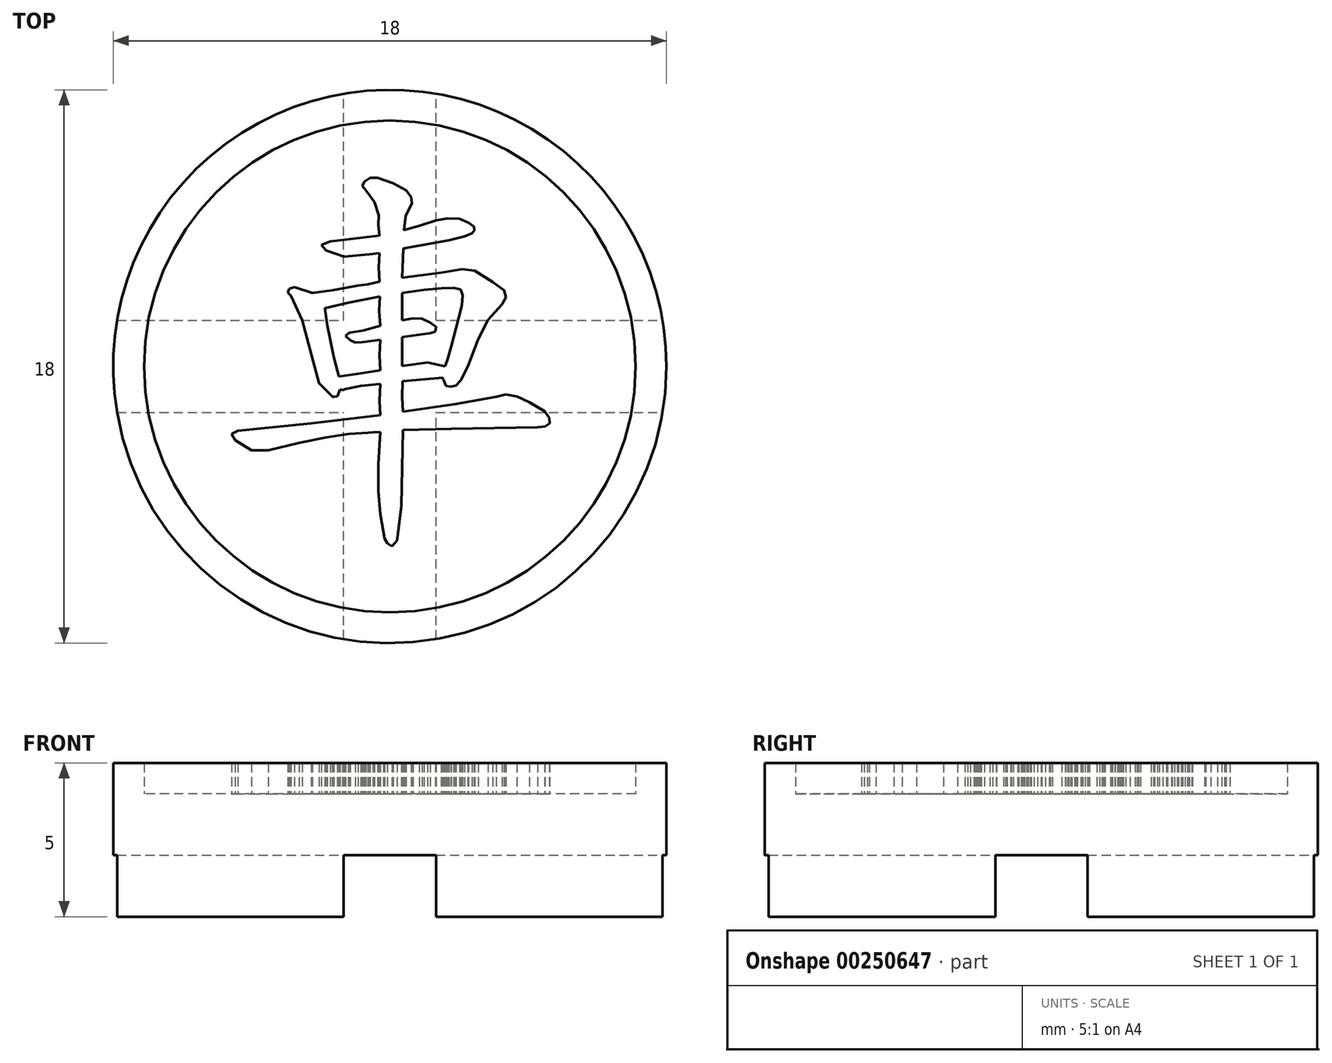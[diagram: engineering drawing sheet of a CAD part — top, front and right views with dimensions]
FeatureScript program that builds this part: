
annotation { "Feature Type Name" : "Feature", "Feature Type Description" : "" }
export const myFeature = defineFeature(function(context is Context, id is Id, definition is map)
    precondition{}
    {
        {
            var Q0;
            Q0=qCreatedBy(makeId("Top.planeOp"),FACE);
            var sketch = newSketch(context, id + "F0", { "sketchPlane" : qUnion([Q0]), "disableImprinting" : false});
            skCircle(sketch, "E0", {"center": v(-31.33, 19.76) * mm, "radius": 9 * mm});
            skSolve(sketch);
        }
        {
            var Q0;
            Q0=qSketchRegion(id+"F0",true);
            extrude(context, id + "F1", {"entities" : qUnion([Q0]), "flatOperationType" : FlatOperationType.REMOVE, "offsetDistance" : 25 * mm, "depth" : 4 * mm, "domain" : OperationDomain.MODEL});
        }
        {
            var Q0;
            Q0=makeQuery(id+"F1.opExtrude","CAP_FACE",FACE,{"disambiguationData":[OSD([sQuery(id+"F0.wireOp",EDGE,"E0")])],"isStart":false});
            var sketch = newSketch(context, id + "F2", { "sketchPlane" : qUnion([Q0]), "disableImprinting" : false});
            skCircle(sketch, "E1", {"center": v(-31.33, 19.76) * mm, "radius": 8 * mm});
            skCircle(sketch, "E2", {"center": v(-31.33, 19.76) * mm, "radius": 9 * mm});
            skSolve(sketch);
        }
        {
            var Q0;
            Q0=makeQuery(id+"F1.opExtrude","CAP_FACE",FACE,{"disambiguationData":[OSD([sQuery(id+"F0.wireOp",EDGE,"E0")])],"isStart":true});
            var sketch = newSketch(context, id + "F3", { "sketchPlane" : qUnion([Q0]), "disableImprinting" : false});
            skLineSegment(sketch, "E3", {"start": v(-31.33, -19.76) * mm, "end": v(-22.33, -19.76) * mm, "construction": true});
            skLineSegment(sketch, "E4", {"start": v(-31.33, -19.76) * mm, "end": v(-31.33, -10.76) * mm, "construction": true});
            skLineSegment(sketch, "E5", {"start": v(-31.33, -19.76) * mm, "end": v(-40.33, -19.76) * mm, "construction": true});
            skLineSegment(sketch, "E6", {"start": v(-31.33, -19.76) * mm, "end": v(-31.33, -28.76) * mm, "construction": true});
            skLineSegment(sketch, "E7.bottom", {"start": v(-40.33, -28.76) * mm, "end": v(-22.33, -28.76) * mm});
            skLineSegment(sketch, "E7.top", {"start": v(-40.33, -10.76) * mm, "end": v(-22.33, -10.76) * mm});
            skLineSegment(sketch, "E7.left", {"start": v(-22.33, -10.76) * mm, "end": v(-22.33, -28.76) * mm});
            skLineSegment(sketch, "E7.right", {"start": v(-40.33, -10.76) * mm, "end": v(-40.33, -28.76) * mm});
            skPoint(sketch, "E8", {"position": v(-31.33, -28.76) * mm});
            skPoint(sketch, "E9", {"position": v(-40.33, -19.76) * mm});
            skPoint(sketch, "E10", {"position": v(-22.33, -19.76) * mm});
            skPoint(sketch, "E11", {"position": v(-31.33, -10.76) * mm});
            skLineSegment(sketch, "E12.bottom", {"start": v(-32.83, -10.76) * mm, "end": v(-29.83, -10.76) * mm});
            skLineSegment(sketch, "E12.top", {"start": v(-32.83, -28.76) * mm, "end": v(-29.83, -28.76) * mm});
            skLineSegment(sketch, "E12.left", {"start": v(-32.83, -10.76) * mm, "end": v(-32.83, -28.76) * mm});
            skLineSegment(sketch, "E12.right", {"start": v(-29.83, -10.76) * mm, "end": v(-29.83, -28.76) * mm});
            skLineSegment(sketch, "E13.bottom", {"start": v(-40.33, -18.26) * mm, "end": v(-22.33, -18.26) * mm});
            skLineSegment(sketch, "E13.top", {"start": v(-40.33, -21.26) * mm, "end": v(-22.33, -21.26) * mm});
            skLineSegment(sketch, "E13.left", {"start": v(-40.33, -18.26) * mm, "end": v(-40.33, -21.26) * mm});
            skLineSegment(sketch, "E13.right", {"start": v(-22.33, -18.26) * mm, "end": v(-22.33, -21.26) * mm});
            skSolve(sketch);
        }
        {
            var Q0;
            {var subQ1=sQuery(id+"F3.wireOp",EDGE,"E12.bottom");var subQ3=makeQuery(id+"F1.opExtrude","CAP_EDGE",EDGE,{"disambiguationData":[OSD([sQuery(id+"F0.wireOp",EDGE,"E0")])],"isStart":true});var subQ4=makeQuery(id+"F3.imprint","INTERSECT",VERTEX,{"derivedFrom":[subQ3,subQ1]});Q0=makeQuery(id+"F3.imprint","IMPRINT",FACE,{"disambiguationData":[TD([[makeQuery(id+"F3.imprint","IMPRINT",EDGE,{"disambiguationData":[TD([[subQ4,1.0]])],"derivedFrom":subQ3}),1.0]])]});}
            var Q1;
            {var subQ1=sQuery(id+"F3.wireOp",EDGE,"E12.bottom");var subQ3=makeQuery(id+"F1.opExtrude","CAP_EDGE",EDGE,{"disambiguationData":[OSD([sQuery(id+"F0.wireOp",EDGE,"E0")])],"isStart":true});var subQ4=makeQuery(id+"F3.imprint","INTERSECT",VERTEX,{"derivedFrom":[subQ3,subQ1]});Q1=makeQuery(id+"F3.imprint","IMPRINT",FACE,{"disambiguationData":[TD([[makeQuery(id+"F3.imprint","IMPRINT",EDGE,{"disambiguationData":[TD([[subQ4,-1.0]])],"derivedFrom":subQ3}),1.0]])]});}
            var Q2;
            {var subQ1=sQuery(id+"F3.wireOp",EDGE,"E12.top");var subQ3=makeQuery(id+"F1.opExtrude","CAP_EDGE",EDGE,{"disambiguationData":[OSD([sQuery(id+"F0.wireOp",EDGE,"E0")])],"isStart":true});var subQ4=makeQuery(id+"F3.imprint","INTERSECT",VERTEX,{"derivedFrom":[subQ3,subQ1]});Q2=makeQuery(id+"F3.imprint","IMPRINT",FACE,{"disambiguationData":[TD([[makeQuery(id+"F3.imprint","IMPRINT",EDGE,{"disambiguationData":[TD([[subQ4,-1.0]])],"derivedFrom":subQ3}),1.0]])]});}
            var Q3;
            {var subQ1=sQuery(id+"F3.wireOp",EDGE,"E12.top");var subQ3=makeQuery(id+"F1.opExtrude","CAP_EDGE",EDGE,{"disambiguationData":[OSD([sQuery(id+"F0.wireOp",EDGE,"E0")])],"isStart":true});var subQ4=makeQuery(id+"F3.imprint","INTERSECT",VERTEX,{"derivedFrom":[subQ3,subQ1]});Q3=makeQuery(id+"F3.imprint","IMPRINT",FACE,{"disambiguationData":[TD([[makeQuery(id+"F3.imprint","IMPRINT",EDGE,{"disambiguationData":[TD([[subQ4,1.0]])],"derivedFrom":subQ3}),1.0]])]});}
            var Q4;
            {var subQ0=sQuery(id+"F3.wireOp",EDGE,"E13.left");var subQ3=makeQuery(id+"F1.opExtrude","CAP_EDGE",EDGE,{"disambiguationData":[OSD([sQuery(id+"F0.wireOp",EDGE,"E0")])],"isStart":true});var subQ5=makeQuery(id+"F3.imprint","INTERSECT",VERTEX,{"derivedFrom":[subQ3,subQ0]});Q4=makeQuery(id+"F3.imprint","IMPRINT",FACE,{"disambiguationData":[TD([[makeQuery(id+"F3.imprint","IMPRINT",EDGE,{"disambiguationData":[TD([[subQ5,-1.0]])],"derivedFrom":subQ3}),1.0]])]});}
            var Q5;
            {var subQ0=sQuery(id+"F3.wireOp",EDGE,"E13.right");var subQ3=makeQuery(id+"F1.opExtrude","CAP_EDGE",EDGE,{"disambiguationData":[OSD([sQuery(id+"F0.wireOp",EDGE,"E0")])],"isStart":true});var subQ5=makeQuery(id+"F3.imprint","INTERSECT",VERTEX,{"derivedFrom":[subQ3,subQ0]});Q5=makeQuery(id+"F3.imprint","IMPRINT",FACE,{"disambiguationData":[TD([[makeQuery(id+"F3.imprint","IMPRINT",EDGE,{"disambiguationData":[TD([[subQ5,1.0]])],"derivedFrom":subQ3}),1.0]])]});}
            var Q6;
            {var subQ0=sQuery(id+"F3.wireOp",EDGE,"E13.left");var subQ3=makeQuery(id+"F1.opExtrude","CAP_EDGE",EDGE,{"disambiguationData":[OSD([sQuery(id+"F0.wireOp",EDGE,"E0")])],"isStart":true});var subQ5=makeQuery(id+"F3.imprint","INTERSECT",VERTEX,{"derivedFrom":[subQ3,subQ0]});Q6=makeQuery(id+"F3.imprint","IMPRINT",FACE,{"disambiguationData":[TD([[makeQuery(id+"F3.imprint","IMPRINT",EDGE,{"disambiguationData":[TD([[subQ5,1.0]])],"derivedFrom":subQ3}),1.0]])]});}
            var Q7;
            {var subQ0=sQuery(id+"F3.wireOp",EDGE,"E13.right");var subQ3=makeQuery(id+"F1.opExtrude","CAP_EDGE",EDGE,{"disambiguationData":[OSD([sQuery(id+"F0.wireOp",EDGE,"E0")])],"isStart":true});var subQ5=makeQuery(id+"F3.imprint","INTERSECT",VERTEX,{"derivedFrom":[subQ3,subQ0]});Q7=makeQuery(id+"F3.imprint","IMPRINT",FACE,{"disambiguationData":[TD([[makeQuery(id+"F3.imprint","IMPRINT",EDGE,{"disambiguationData":[TD([[subQ5,-1.0]])],"derivedFrom":subQ3}),1.0]])]});}
            var Q8;
            {var subQ3=makeQuery(id+"F1.opExtrude","CAP_EDGE",EDGE,{"disambiguationData":[OSD([sQuery(id+"F0.wireOp",EDGE,"E0")])],"isStart":true});var subQ5=sQuery(id+"F3.wireOp",EDGE,"E12.left");var subQ8=makeQuery(id+"F3.imprint","INTERSECT",VERTEX,{"disambiguationData":[OD(1.0)],"derivedFrom":[subQ3,subQ5]});Q8=makeQuery(id+"F3.imprint","IMPRINT",FACE,{"disambiguationData":[TD([[makeQuery(id+"F3.imprint","IMPRINT",EDGE,{"disambiguationData":[TD([[subQ8,-1.0]])],"derivedFrom":subQ3}),1.0]])]});}
            var Q9;
            {var subQ3=makeQuery(id+"F1.opExtrude","CAP_EDGE",EDGE,{"disambiguationData":[OSD([sQuery(id+"F0.wireOp",EDGE,"E0")])],"isStart":true});var subQ5=sQuery(id+"F3.wireOp",EDGE,"E12.right");var subQ8=makeQuery(id+"F3.imprint","INTERSECT",VERTEX,{"disambiguationData":[OD(1.0)],"derivedFrom":[subQ3,subQ5]});Q9=makeQuery(id+"F3.imprint","IMPRINT",FACE,{"disambiguationData":[TD([[makeQuery(id+"F3.imprint","IMPRINT",EDGE,{"disambiguationData":[TD([[subQ8,1.0]])],"derivedFrom":subQ3}),1.0]])]});}
            var Q10;
            {var subQ3=makeQuery(id+"F1.opExtrude","CAP_EDGE",EDGE,{"disambiguationData":[OSD([sQuery(id+"F0.wireOp",EDGE,"E0")])],"isStart":true});var subQ5=sQuery(id+"F3.wireOp",EDGE,"E12.left");var subQ8=makeQuery(id+"F3.imprint","INTERSECT",VERTEX,{"disambiguationData":[OD(0.0)],"derivedFrom":[subQ3,subQ5]});Q10=makeQuery(id+"F3.imprint","IMPRINT",FACE,{"disambiguationData":[TD([[makeQuery(id+"F3.imprint","IMPRINT",EDGE,{"disambiguationData":[TD([[subQ8,1.0]])],"derivedFrom":subQ3}),1.0]])]});}
            var Q11;
            {var subQ3=makeQuery(id+"F1.opExtrude","CAP_EDGE",EDGE,{"disambiguationData":[OSD([sQuery(id+"F0.wireOp",EDGE,"E0")])],"isStart":true});var subQ5=sQuery(id+"F3.wireOp",EDGE,"E12.right");var subQ8=makeQuery(id+"F3.imprint","INTERSECT",VERTEX,{"disambiguationData":[OD(0.0)],"derivedFrom":[subQ3,subQ5]});Q11=makeQuery(id+"F3.imprint","IMPRINT",FACE,{"disambiguationData":[TD([[makeQuery(id+"F3.imprint","IMPRINT",EDGE,{"disambiguationData":[TD([[subQ8,-1.0]])],"derivedFrom":subQ3}),1.0]])]});}
            var Q12;
            {var subQ2=sQuery(id+"F3.wireOp",EDGE,"E12.left");var subQ4=sQuery(id+"F3.wireOp",EDGE,"E13.bottom");var subQ8=makeQuery(id+"F3.imprint","INTERSECT",VERTEX,{"derivedFrom":[subQ2,subQ4]});Q12=makeQuery(id+"F3.imprint","IMPRINT",FACE,{"disambiguationData":[TD([[makeQuery(id+"F3.imprint","IMPRINT",EDGE,{"disambiguationData":[TD([[subQ8,1.0]])],"derivedFrom":subQ2}),1.0]])]});}
            var Q13;
            {var subQ1=sQuery(id+"F3.wireOp",EDGE,"E12.left");var subQ5=sQuery(id+"F3.wireOp",EDGE,"E13.bottom");var subQ6=makeQuery(id+"F3.imprint","INTERSECT",VERTEX,{"derivedFrom":[subQ1,subQ5]});Q13=makeQuery(id+"F3.imprint","IMPRINT",FACE,{"disambiguationData":[TD([[makeQuery(id+"F3.imprint","IMPRINT",EDGE,{"disambiguationData":[TD([[subQ6,-1.0]])],"derivedFrom":subQ1}),-1.0]])]});}
            var Q14;
            {var subQ0=sQuery(id+"F3.wireOp",EDGE,"E13.top");var subQ1=sQuery(id+"F3.wireOp",EDGE,"E12.left");var subQ2=makeQuery(id+"F3.imprint","INTERSECT",VERTEX,{"derivedFrom":[subQ1,subQ0]});Q14=makeQuery(id+"F3.imprint","IMPRINT",FACE,{"disambiguationData":[TD([[makeQuery(id+"F3.imprint","IMPRINT",EDGE,{"disambiguationData":[TD([[subQ2,-1.0]])],"derivedFrom":subQ1}),1.0]])]});}
            var Q15;
            {var subQ2=sQuery(id+"F3.wireOp",EDGE,"E13.bottom");var subQ5=sQuery(id+"F3.wireOp",EDGE,"E12.right");var subQ8=makeQuery(id+"F3.imprint","INTERSECT",VERTEX,{"derivedFrom":[subQ5,subQ2]});Q15=makeQuery(id+"F3.imprint","IMPRINT",FACE,{"disambiguationData":[TD([[makeQuery(id+"F3.imprint","IMPRINT",EDGE,{"disambiguationData":[TD([[subQ8,-1.0]])],"derivedFrom":subQ5}),1.0]])]});}
            var Q16;
            {var subQ0=sQuery(id+"F3.wireOp",EDGE,"E13.bottom");var subQ1=sQuery(id+"F3.wireOp",EDGE,"E12.left");var subQ2=makeQuery(id+"F3.imprint","INTERSECT",VERTEX,{"derivedFrom":[subQ1,subQ0]});Q16=makeQuery(id+"F3.imprint","IMPRINT",FACE,{"disambiguationData":[TD([[makeQuery(id+"F3.imprint","IMPRINT",EDGE,{"disambiguationData":[TD([[subQ2,-1.0]])],"derivedFrom":subQ1}),1.0]])]});}
            extrude(context, id + "F4", {"entities" : qUnion([Q0, Q1, Q2, Q3, Q4, Q5, Q6, Q7, Q8, Q9, Q10, Q11, Q12, Q13, Q14, Q15, Q16]), "operationType" : NewBodyOperationType.REMOVE, "oppositeDirection" : true, "depth" : 2 * mm});
        }
        {
            var Q0;
            Q0=qSketchRegion(id+"F2",true);
            var Q1;
            Q1=makeQuery(id+"F2.imprint","IMPRINT",FACE,{"disambiguationData":[TD([[makeQuery(id+"F2.imprint","IMPRINT",EDGE,{"derivedFrom":sQuery(id+"F2.wireOp",EDGE,"hKqnuJLd-dfdz-vJIs-yDKo-c4hLNRw30SuP")}),-1.0]])]});
            extrude(context, id + "F5", {"entities" : qUnion([Q0, Q1]), "operationType" : NewBodyOperationType.ADD, "depth" : 1 * mm});
        }
        {
            var Q0;
            Q0=makeQuery(id+"F1.opExtrude","CAP_FACE",FACE,{"disambiguationData":[OSD([sQuery(id+"F0.wireOp",EDGE,"E0")])],"isStart":false});
            var sketch = newSketch(context, id + "F6", { "sketchPlane" : qUnion([Q0])});
            skLineSegment(sketch, "E14", {"start": v(-31.65, 17.63) * mm, "end": v(-31.7, 16.58) * mm});
            skLineSegment(sketch, "E15", {"start": v(-31.7, 16.58) * mm, "end": v(-31.7, 15.7) * mm});
            skLineSegment(sketch, "E16", {"start": v(-31.7, 15.7) * mm, "end": v(-31.64, 14.96) * mm});
            skLineSegment(sketch, "E17", {"start": v(-31.64, 14.96) * mm, "end": v(-31.55, 14.38) * mm});
            skLineSegment(sketch, "E18", {"start": v(-31.55, 14.38) * mm, "end": v(-31.5, 14.16) * mm});
            skLineSegment(sketch, "E19", {"start": v(-31.5, 14.16) * mm, "end": v(-31.4, 14) * mm});
            skLineSegment(sketch, "E20", {"start": v(-31.4, 14) * mm, "end": v(-31.26, 13.9) * mm});
            skLineSegment(sketch, "E21", {"start": v(-31.26, 13.9) * mm, "end": v(-31.1, 14.1) * mm});
            skLineSegment(sketch, "E22", {"start": v(-31.1, 14.1) * mm, "end": v(-30.96, 15.23) * mm});
            skLineSegment(sketch, "E23", {"start": v(-30.96, 15.23) * mm, "end": v(-30.9, 17.69) * mm});
            skLineSegment(sketch, "E24", {"start": v(-30.9, 17.69) * mm, "end": v(-29.33, 17.73) * mm});
            skLineSegment(sketch, "E25", {"start": v(-29.33, 17.73) * mm, "end": v(-26.52, 17.78) * mm});
            skLineSegment(sketch, "E26", {"start": v(-26.52, 17.78) * mm, "end": v(-26.28, 17.8) * mm});
            skLineSegment(sketch, "E27", {"start": v(-26.28, 17.8) * mm, "end": v(-26.13, 17.9) * mm});
            skLineSegment(sketch, "E28", {"start": v(-26.13, 17.9) * mm, "end": v(-26.14, 18.08) * mm});
            skLineSegment(sketch, "E29", {"start": v(-26.14, 18.08) * mm, "end": v(-26.3, 18.3) * mm});
            skLineSegment(sketch, "E30", {"start": v(-26.3, 18.3) * mm, "end": v(-26.78, 18.6) * mm});
            skLineSegment(sketch, "E31", {"start": v(-26.78, 18.6) * mm, "end": v(-27.2, 18.78) * mm});
            skLineSegment(sketch, "E32", {"start": v(-27.2, 18.78) * mm, "end": v(-27.56, 18.84) * mm});
            skLineSegment(sketch, "E33", {"start": v(-27.56, 18.84) * mm, "end": v(-27.87, 18.77) * mm});
            skLineSegment(sketch, "E34", {"start": v(-27.87, 18.77) * mm, "end": v(-29.23, 18.53) * mm});
            skLineSegment(sketch, "E35", {"start": v(-29.23, 18.53) * mm, "end": v(-30.9, 18.3) * mm});
            skLineSegment(sketch, "E36", {"start": v(-30.9, 18.3) * mm, "end": v(-30.93, 18.76) * mm});
            skLineSegment(sketch, "E37", {"start": v(-30.93, 18.76) * mm, "end": v(-30.92, 19.28) * mm});
            skLineSegment(sketch, "E38", {"start": v(-30.92, 19.28) * mm, "end": v(-29.6, 19.4) * mm});
            skLineSegment(sketch, "E39", {"start": v(-29.6, 19.4) * mm, "end": v(-29.61, 19.33) * mm});
            skLineSegment(sketch, "E40", {"start": v(-29.61, 19.33) * mm, "end": v(-29.58, 19.31) * mm});
            skLineSegment(sketch, "E41", {"start": v(-29.58, 19.31) * mm, "end": v(-29.51, 19.13) * mm});
            skLineSegment(sketch, "E42", {"start": v(-29.51, 19.13) * mm, "end": v(-29.34, 19.1) * mm});
            skLineSegment(sketch, "E43", {"start": v(-29.34, 19.1) * mm, "end": v(-29.18, 19.15) * mm});
            skLineSegment(sketch, "E44", {"start": v(-29.18, 19.15) * mm, "end": v(-29.03, 19.31) * mm});
            skLineSegment(sketch, "E45", {"start": v(-29.03, 19.31) * mm, "end": v(-28.8, 19.75) * mm});
            skLineSegment(sketch, "E46", {"start": v(-28.8, 19.75) * mm, "end": v(-28.46, 20.65) * mm});
            skLineSegment(sketch, "E47", {"start": v(-28.46, 20.65) * mm, "end": v(-28.14, 21.28) * mm});
            skLineSegment(sketch, "E48", {"start": v(-28.14, 21.28) * mm, "end": v(-27.68, 21.79) * mm});
            skLineSegment(sketch, "E49", {"start": v(-27.68, 21.79) * mm, "end": v(-27.55, 22) * mm});
            skLineSegment(sketch, "E50", {"start": v(-27.55, 22) * mm, "end": v(-27.62, 22.24) * mm});
            skLineSegment(sketch, "E51", {"start": v(-27.62, 22.24) * mm, "end": v(-27.98, 22.5) * mm});
            skLineSegment(sketch, "E52", {"start": v(-27.98, 22.5) * mm, "end": v(-28.57, 22.88) * mm});
            skLineSegment(sketch, "E53", {"start": v(-28.57, 22.88) * mm, "end": v(-28.97, 22.93) * mm});
            skLineSegment(sketch, "E54", {"start": v(-28.97, 22.93) * mm, "end": v(-29.66, 22.81) * mm});
            skLineSegment(sketch, "E55", {"start": v(-29.66, 22.81) * mm, "end": v(-30.93, 22.64) * mm});
            skLineSegment(sketch, "E56", {"start": v(-30.93, 22.64) * mm, "end": v(-30.9, 23.6) * mm});
            skLineSegment(sketch, "E57", {"start": v(-30.9, 23.6) * mm, "end": v(-29.4, 23.87) * mm});
            skLineSegment(sketch, "E58", {"start": v(-29.4, 23.87) * mm, "end": v(-28.9, 24) * mm});
            skLineSegment(sketch, "E59", {"start": v(-28.9, 24) * mm, "end": v(-28.66, 24.1) * mm});
            skLineSegment(sketch, "E60", {"start": v(-28.66, 24.1) * mm, "end": v(-28.59, 24.18) * mm});
            skLineSegment(sketch, "E61", {"start": v(-28.59, 24.18) * mm, "end": v(-28.6, 24.3) * mm});
            skLineSegment(sketch, "E62", {"start": v(-28.6, 24.3) * mm, "end": v(-28.77, 24.44) * mm});
            skLineSegment(sketch, "E63", {"start": v(-28.77, 24.44) * mm, "end": v(-29.06, 24.56) * mm});
            skLineSegment(sketch, "E64", {"start": v(-29.06, 24.56) * mm, "end": v(-29.46, 24.58) * mm});
            skLineSegment(sketch, "E65", {"start": v(-29.46, 24.58) * mm, "end": v(-29.83, 24.51) * mm});
            skLineSegment(sketch, "E66", {"start": v(-29.83, 24.51) * mm, "end": v(-30.37, 24.34) * mm});
            skLineSegment(sketch, "E67", {"start": v(-30.37, 24.34) * mm, "end": v(-30.88, 24.2) * mm});
            skLineSegment(sketch, "E68", {"start": v(-30.88, 24.2) * mm, "end": v(-30.9, 24.18) * mm});
            skLineSegment(sketch, "E69", {"start": v(-30.9, 24.18) * mm, "end": v(-30.87, 24.22) * mm});
            skLineSegment(sketch, "E70", {"start": v(-30.87, 24.22) * mm, "end": v(-30.81, 24.66) * mm});
            skLineSegment(sketch, "E71", {"start": v(-30.81, 24.66) * mm, "end": v(-30.62, 25.07) * mm});
            skLineSegment(sketch, "E72", {"start": v(-30.62, 25.07) * mm, "end": v(-30.64, 25.28) * mm});
            skLineSegment(sketch, "E73", {"start": v(-30.64, 25.28) * mm, "end": v(-30.8, 25.5) * mm});
            skLineSegment(sketch, "E74", {"start": v(-30.8, 25.5) * mm, "end": v(-31.23, 25.72) * mm});
            skLineSegment(sketch, "E75", {"start": v(-31.23, 25.72) * mm, "end": v(-31.72, 25.9) * mm});
            skLineSegment(sketch, "E76", {"start": v(-31.72, 25.9) * mm, "end": v(-31.98, 25.9) * mm});
            skLineSegment(sketch, "E77", {"start": v(-31.98, 25.9) * mm, "end": v(-32.16, 25.77) * mm});
            skLineSegment(sketch, "E78", {"start": v(-32.16, 25.77) * mm, "end": v(-32.22, 25.63) * mm});
            skLineSegment(sketch, "E79", {"start": v(-32.22, 25.63) * mm, "end": v(-32.11, 25.5) * mm});
            skLineSegment(sketch, "E80", {"start": v(-32.11, 25.5) * mm, "end": v(-31.83, 25.11) * mm});
            skLineSegment(sketch, "E81", {"start": v(-31.83, 25.11) * mm, "end": v(-31.69, 24.67) * mm});
            skLineSegment(sketch, "E82", {"start": v(-31.69, 24.67) * mm, "end": v(-31.7, 24.37) * mm});
            skLineSegment(sketch, "E83", {"start": v(-31.7, 24.37) * mm, "end": v(-31.67, 24.02) * mm});
            skLineSegment(sketch, "E84", {"start": v(-31.67, 24.02) * mm, "end": v(-33.27, 23.82) * mm});
            skLineSegment(sketch, "E85", {"start": v(-33.27, 23.82) * mm, "end": v(-33.56, 23.72) * mm});
            skLineSegment(sketch, "E86", {"start": v(-33.56, 23.72) * mm, "end": v(-33.4, 23.53) * mm});
            skLineSegment(sketch, "E87", {"start": v(-33.4, 23.53) * mm, "end": v(-32.82, 23.33) * mm});
            skLineSegment(sketch, "E88", {"start": v(-32.82, 23.33) * mm, "end": v(-32, 23.4) * mm});
            skLineSegment(sketch, "E89", {"start": v(-32, 23.4) * mm, "end": v(-31.67, 23.44) * mm});
            skLineSegment(sketch, "E90", {"start": v(-31.67, 23.44) * mm, "end": v(-31.7, 23) * mm});
            skLineSegment(sketch, "E91", {"start": v(-31.7, 23) * mm, "end": v(-31.67, 22.51) * mm});
            skLineSegment(sketch, "E92", {"start": v(-31.67, 22.51) * mm, "end": v(-32.05, 22.43) * mm});
            skLineSegment(sketch, "E93", {"start": v(-32.05, 22.43) * mm, "end": v(-32.36, 22.39) * mm});
            skLineSegment(sketch, "E94", {"start": v(-32.36, 22.39) * mm, "end": v(-33.19, 22.24) * mm});
            skLineSegment(sketch, "E95", {"start": v(-33.19, 22.24) * mm, "end": v(-33.85, 22.15) * mm});
            skLineSegment(sketch, "E96", {"start": v(-33.85, 22.15) * mm, "end": v(-34.44, 22.34) * mm});
            skLineSegment(sketch, "E97", {"start": v(-34.44, 22.34) * mm, "end": v(-34.6, 22.29) * mm});
            skLineSegment(sketch, "E98", {"start": v(-34.6, 22.29) * mm, "end": v(-34.65, 22.17) * mm});
            skLineSegment(sketch, "E99", {"start": v(-34.65, 22.17) * mm, "end": v(-34.55, 22.06) * mm});
            skLineSegment(sketch, "E100", {"start": v(-34.55, 22.06) * mm, "end": v(-34.18, 21.27) * mm});
            skLineSegment(sketch, "E101", {"start": v(-34.18, 21.27) * mm, "end": v(-33.82, 19.93) * mm});
            skLineSegment(sketch, "E102", {"start": v(-33.82, 19.93) * mm, "end": v(-33.63, 19.21) * mm});
            skLineSegment(sketch, "E103", {"start": v(-33.63, 19.21) * mm, "end": v(-33.2, 18.78) * mm});
            skLineSegment(sketch, "E104", {"start": v(-33.2, 18.78) * mm, "end": v(-33.2, 18.76) * mm});
            skLineSegment(sketch, "E105", {"start": v(-33.2, 18.76) * mm, "end": v(-33.17, 18.77) * mm});
            skLineSegment(sketch, "E106", {"start": v(-33.17, 18.77) * mm, "end": v(-33.03, 18.79) * mm});
            skLineSegment(sketch, "E107", {"start": v(-33.03, 18.79) * mm, "end": v(-32.95, 19) * mm});
            skLineSegment(sketch, "E108", {"start": v(-32.95, 19) * mm, "end": v(-32.88, 18.99) * mm});
            skLineSegment(sketch, "E109", {"start": v(-32.88, 18.99) * mm, "end": v(-32.77, 19.02) * mm});
            skLineSegment(sketch, "E110", {"start": v(-32.77, 19.02) * mm, "end": v(-32.28, 19.12) * mm});
            skLineSegment(sketch, "E111", {"start": v(-32.28, 19.12) * mm, "end": v(-31.64, 19.2) * mm});
            skLineSegment(sketch, "E112", {"start": v(-31.64, 19.2) * mm, "end": v(-31.66, 18.65) * mm});
            skLineSegment(sketch, "E113", {"start": v(-31.66, 18.65) * mm, "end": v(-31.65, 18.18) * mm});
            skLineSegment(sketch, "E114", {"start": v(-31.65, 18.18) * mm, "end": v(-33.89, 17.9) * mm});
            skLineSegment(sketch, "E115", {"start": v(-33.89, 17.9) * mm, "end": v(-36.27, 17.66) * mm});
            skLineSegment(sketch, "E116", {"start": v(-36.27, 17.66) * mm, "end": v(-36.48, 17.57) * mm});
            skLineSegment(sketch, "E117", {"start": v(-36.48, 17.57) * mm, "end": v(-36.36, 17.36) * mm});
            skLineSegment(sketch, "E118", {"start": v(-36.36, 17.36) * mm, "end": v(-35.83, 17.03) * mm});
            skLineSegment(sketch, "E119", {"start": v(-35.83, 17.03) * mm, "end": v(-35.28, 17.03) * mm});
            skLineSegment(sketch, "E120", {"start": v(-35.28, 17.03) * mm, "end": v(-34.28, 17.27) * mm});
            skLineSegment(sketch, "E121", {"start": v(-34.28, 17.27) * mm, "end": v(-33.4, 17.45) * mm});
            skLineSegment(sketch, "E122", {"start": v(-33.4, 17.45) * mm, "end": v(-32.65, 17.56) * mm});
            skLineSegment(sketch, "E123", {"start": v(-32.65, 17.56) * mm, "end": v(-32.04, 17.6) * mm});
            skLineSegment(sketch, "E124", {"start": v(-32.04, 17.6) * mm, "end": v(-31.88, 17.62) * mm});
            skLineSegment(sketch, "E125", {"start": v(-31.88, 17.62) * mm, "end": v(-31.65, 17.63) * mm});
            skLineSegment(sketch, "E126", {"start": v(-30.93, 20.72) * mm, "end": v(-30.02, 20.84) * mm});
            skLineSegment(sketch, "E127", {"start": v(-30.02, 20.84) * mm, "end": v(-29.85, 20.9) * mm});
            skLineSegment(sketch, "E128", {"start": v(-29.85, 20.9) * mm, "end": v(-29.83, 21.05) * mm});
            skLineSegment(sketch, "E129", {"start": v(-29.83, 21.05) * mm, "end": v(-30.02, 21.18) * mm});
            skLineSegment(sketch, "E130", {"start": v(-30.02, 21.18) * mm, "end": v(-30.28, 21.3) * mm});
            skLineSegment(sketch, "E131", {"start": v(-30.28, 21.3) * mm, "end": v(-30.57, 21.32) * mm});
            skLineSegment(sketch, "E132", {"start": v(-30.57, 21.32) * mm, "end": v(-30.93, 21.26) * mm});
            skLineSegment(sketch, "E133", {"start": v(-30.93, 21.26) * mm, "end": v(-30.93, 22.15) * mm});
            skLineSegment(sketch, "E134", {"start": v(-30.93, 22.15) * mm, "end": v(-30.21, 22.25) * mm});
            skLineSegment(sketch, "E135", {"start": v(-30.21, 22.25) * mm, "end": v(-29.65, 22.3) * mm});
            skLineSegment(sketch, "E136", {"start": v(-29.65, 22.3) * mm, "end": v(-29.26, 22.31) * mm});
            skLineSegment(sketch, "E137", {"start": v(-29.26, 22.31) * mm, "end": v(-29.03, 22.26) * mm});
            skLineSegment(sketch, "E138", {"start": v(-29.03, 22.26) * mm, "end": v(-28.96, 22.07) * mm});
            skLineSegment(sketch, "E139", {"start": v(-28.96, 22.07) * mm, "end": v(-28.99, 21.74) * mm});
            skLineSegment(sketch, "E140", {"start": v(-28.99, 21.74) * mm, "end": v(-29.18, 21) * mm});
            skLineSegment(sketch, "E141", {"start": v(-29.18, 21) * mm, "end": v(-29.33, 20.43) * mm});
            skLineSegment(sketch, "E142", {"start": v(-29.33, 20.43) * mm, "end": v(-29.44, 20.02) * mm});
            skLineSegment(sketch, "E143", {"start": v(-29.44, 20.02) * mm, "end": v(-29.54, 19.76) * mm});
            skLineSegment(sketch, "E144", {"start": v(-29.54, 19.76) * mm, "end": v(-30.1, 19.89) * mm});
            skLineSegment(sketch, "E145", {"start": v(-30.1, 19.89) * mm, "end": v(-30.93, 19.77) * mm});
            skLineSegment(sketch, "E146", {"start": v(-30.93, 19.77) * mm, "end": v(-30.93, 20.72) * mm});
            skLineSegment(sketch, "E147", {"start": v(-31.65, 21.08) * mm, "end": v(-32.2, 20.94) * mm});
            skLineSegment(sketch, "E148", {"start": v(-32.2, 20.94) * mm, "end": v(-32.65, 20.85) * mm});
            skLineSegment(sketch, "E149", {"start": v(-32.65, 20.85) * mm, "end": v(-32.77, 20.75) * mm});
            skLineSegment(sketch, "E150", {"start": v(-32.77, 20.75) * mm, "end": v(-32.62, 20.62) * mm});
            skLineSegment(sketch, "E151", {"start": v(-32.62, 20.62) * mm, "end": v(-32.46, 20.54) * mm});
            skLineSegment(sketch, "E152", {"start": v(-32.46, 20.54) * mm, "end": v(-32.23, 20.55) * mm});
            skLineSegment(sketch, "E153", {"start": v(-32.23, 20.55) * mm, "end": v(-31.65, 20.63) * mm});
            skLineSegment(sketch, "E154", {"start": v(-31.65, 20.63) * mm, "end": v(-31.67, 20.12) * mm});
            skLineSegment(sketch, "E155", {"start": v(-31.67, 20.12) * mm, "end": v(-31.64, 19.64) * mm});
            skLineSegment(sketch, "E156", {"start": v(-31.64, 19.64) * mm, "end": v(-32.36, 19.52) * mm});
            skLineSegment(sketch, "E157", {"start": v(-32.36, 19.52) * mm, "end": v(-33, 19.44) * mm});
            skLineSegment(sketch, "E158", {"start": v(-33, 19.44) * mm, "end": v(-33.16, 20.05) * mm});
            skLineSegment(sketch, "E159", {"start": v(-33.16, 20.05) * mm, "end": v(-33.36, 21.11) * mm});
            skLineSegment(sketch, "E160", {"start": v(-33.36, 21.11) * mm, "end": v(-33.45, 21.66) * mm});
            skLineSegment(sketch, "E161", {"start": v(-33.45, 21.66) * mm, "end": v(-32.68, 21.84) * mm});
            skLineSegment(sketch, "E162", {"start": v(-32.68, 21.84) * mm, "end": v(-31.66, 22.04) * mm});
            skLineSegment(sketch, "E163", {"start": v(-31.66, 22.04) * mm, "end": v(-31.68, 21.57) * mm});
            skLineSegment(sketch, "E164", {"start": v(-31.68, 21.57) * mm, "end": v(-31.65, 21.08) * mm});
            skSolve(sketch);
        }
        {
            var Q0;
            Q0 = qSketchRegion(id + "F6", true);
            extrude(context, id + "F7", {"entities" : qUnion([Q0]), "operationType" : NewBodyOperationType.ADD, "depth" : 1 * mm});
        }
    });
